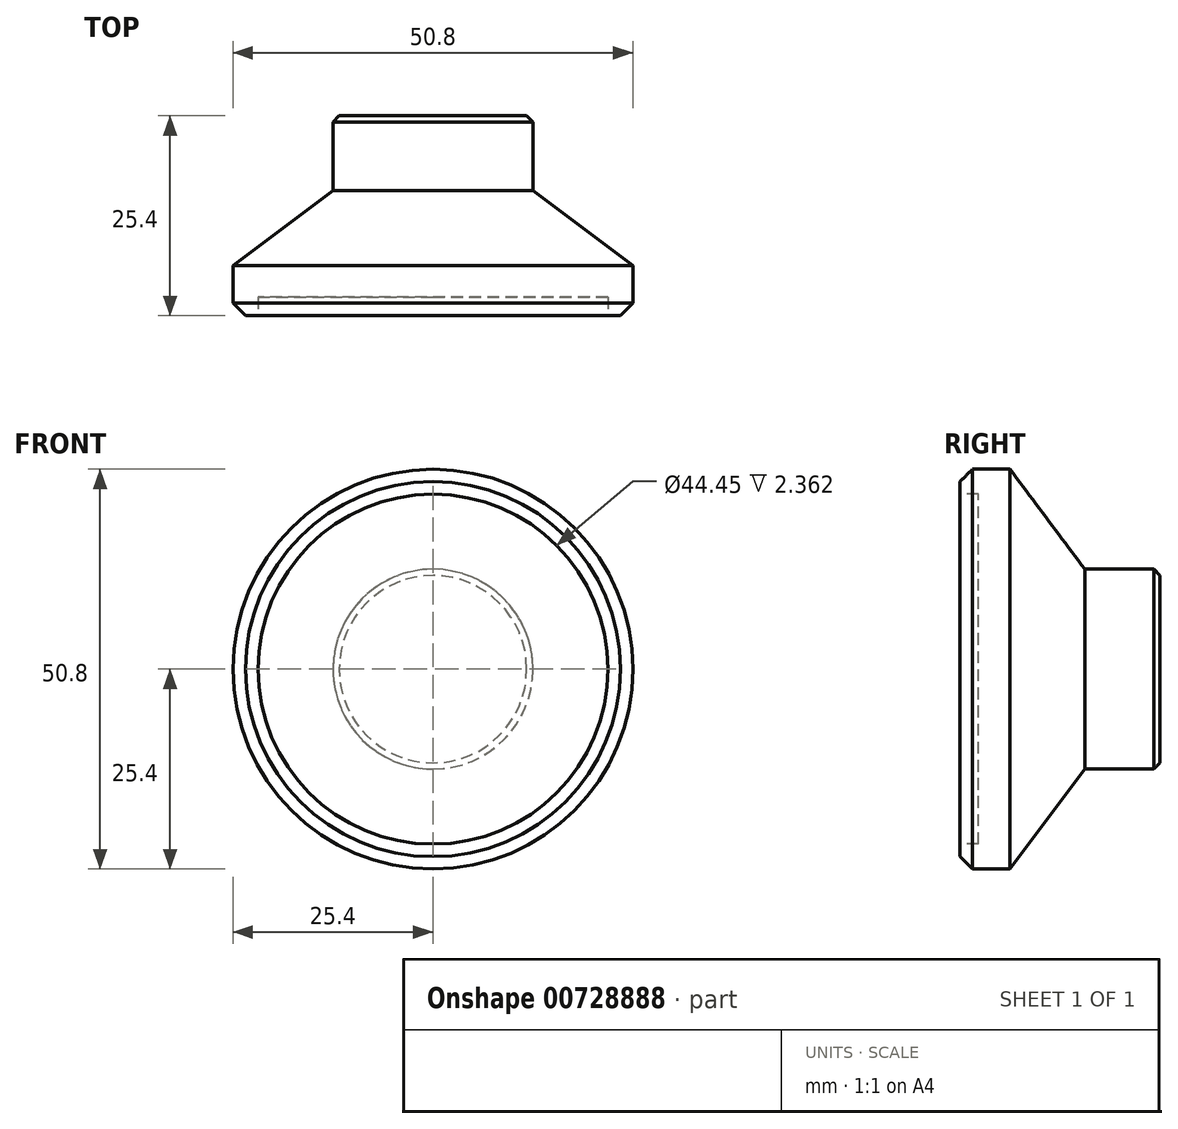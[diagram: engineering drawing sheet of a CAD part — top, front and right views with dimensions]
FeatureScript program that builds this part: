
annotation { "Feature Type Name" : "Feature", "Feature Type Description" : "" }
export const myFeature = defineFeature(function(context is Context, id is Id, definition is map)
    precondition{}
    {
        {
            var Q0;
            Q0=qCreatedBy(makeId("Right.planeOp"),FACE);
            var sketch = newSketch(context, id + "F0", { "sketchPlane" : qUnion([Q0])});
            skLineSegment(sketch, "E0", {"start": v(0, 0) * mm, "end": v(0, 25.4) * mm});
            skLineSegment(sketch, "E1", {"start": v(0, 25.4) * mm, "end": v(6.35, 25.4) * mm});
            skLineSegment(sketch, "E2", {"start": v(6.35, 25.4) * mm, "end": v(15.88, 12.7) * mm});
            skLineSegment(sketch, "E3", {"start": v(15.88, 12.7) * mm, "end": v(25.4, 12.7) * mm});
            skLineSegment(sketch, "E4", {"start": v(25.4, 12.7) * mm, "end": v(25.4, 0) * mm});
            skLineSegment(sketch, "E5", {"start": v(25.4, 0) * mm, "end": v(0, 0) * mm});
            skSolve(sketch);
        }
        {
            var Q0;
            Q0 = qSketchRegion(id + "F0", true);
            var Q1;
            Q1=sQuery(id+"F0.wireOp",EDGE,"E5");
            revolve(context, id + "F1", {"surfaceOperationType" : NewSurfaceOperationType.NEW, "entities" : qUnion([Q0]), "axis" : qUnion([Q1]), "revolveType" : RevolveType.FULL});
        }
        {
            var Q0;
            Q0=makeQuery(id+"F1.opRevolve","SWEPT_EDGE",EDGE,{"disambiguationData":[OSD([sQuery(id+"F0.wireOp",EDGE,"E3"),sQuery(id+"F0.wireOp",EDGE,"E4")])]});
            chamfer(context, id + "F2", {"entities" : qUnion([Q0]), "width" : 0.8 * mm, "tangentPropagation" : true});
        }
        {
            var Q0;
            Q0=makeQuery(id+"F1.opRevolve","SWEPT_EDGE",EDGE,{"disambiguationData":[OSD([sQuery(id+"F0.wireOp",EDGE,"E0"),sQuery(id+"F0.wireOp",EDGE,"E1")])]});
            chamfer(context, id + "F3", {"entities" : qUnion([Q0]), "width" : 1.59 * mm, "tangentPropagation" : true});
        }
        {
            var Q0;
            Q0=makeQuery(id+"F1.opRevolve","SWEPT_FACE",FACE,{"disambiguationData":[OSD([sQuery(id+"F0.wireOp",EDGE,"E0")])]});
            var sketch = newSketch(context, id + "F4", { "sketchPlane" : qUnion([Q0])});
            skCircle(sketch, "E6", {"center": v(0, 0) * mm, "radius": 22.23 * mm});
            skSolve(sketch);
        }
        {
            var Q0;
            Q0 = qSketchRegion(id + "F4", true);
            extrude(context, id + "F5", {"entities" : qUnion([Q0]), "operationType" : NewBodyOperationType.REMOVE, "oppositeDirection" : true, "depth" : 2.36 * mm, "offsetDistance" : 25.4 * mm});
        }
    });
